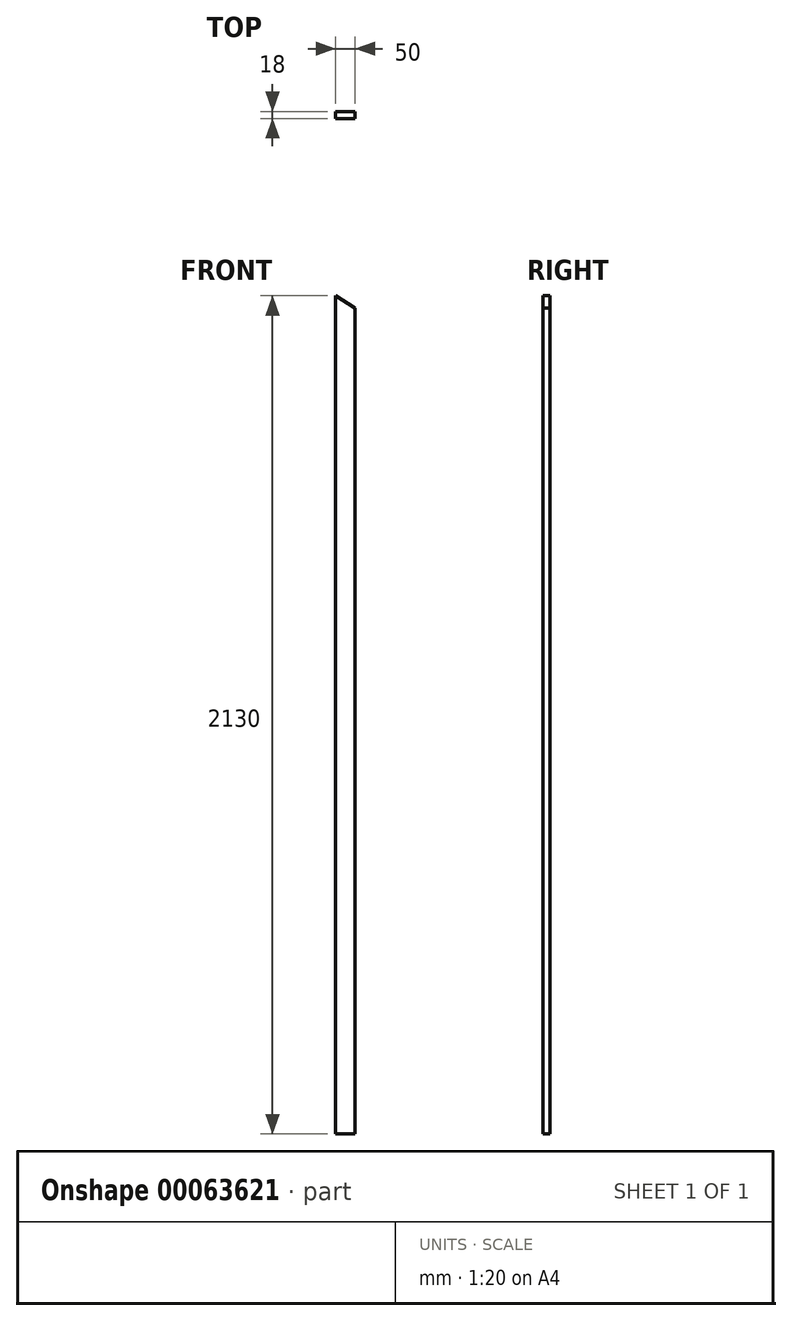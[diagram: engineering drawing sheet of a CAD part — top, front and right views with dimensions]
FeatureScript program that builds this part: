
annotation { "Feature Type Name" : "Feature", "Feature Type Description" : "" }
export const myFeature = defineFeature(function(context is Context, id is Id, definition is map)
    precondition{}
    {
        {
            var Q0;
            Q0=qCreatedBy(makeId("Front.planeOp"),FACE);
            var sketch = newSketch(context, id + "F0", { "sketchPlane" : qUnion([Q0])});
            skLineSegment(sketch, "E0.top", {"start": v(0, -2130) * mm, "end": v(50, -2130) * mm});
            skLineSegment(sketch, "E0.left", {"start": v(0, 0) * mm, "end": v(0, -2130) * mm});
            skLineSegment(sketch, "E0.right", {"start": v(50, -31.62) * mm, "end": v(50, -2130) * mm});
            skLineSegment(sketch, "E1", {"start": v(0, 0) * mm, "end": v(50, -31.62) * mm});
            skSolve(sketch);
        }
        {
            var Q0;
            Q0=makeQuery(id+"F0.imprint","IMPRINT",FACE,{"disambiguationData":[TD([[makeQuery(id+"F0.imprint","IMPRINT",EDGE,{"derivedFrom":sQuery(id+"F0.wireOp",EDGE,"E0.top")}),1.0]])]});
            extrude(context, id + "F1", {"entities" : qUnion([Q0]), "depth" : 18 * mm});
        }
    });
